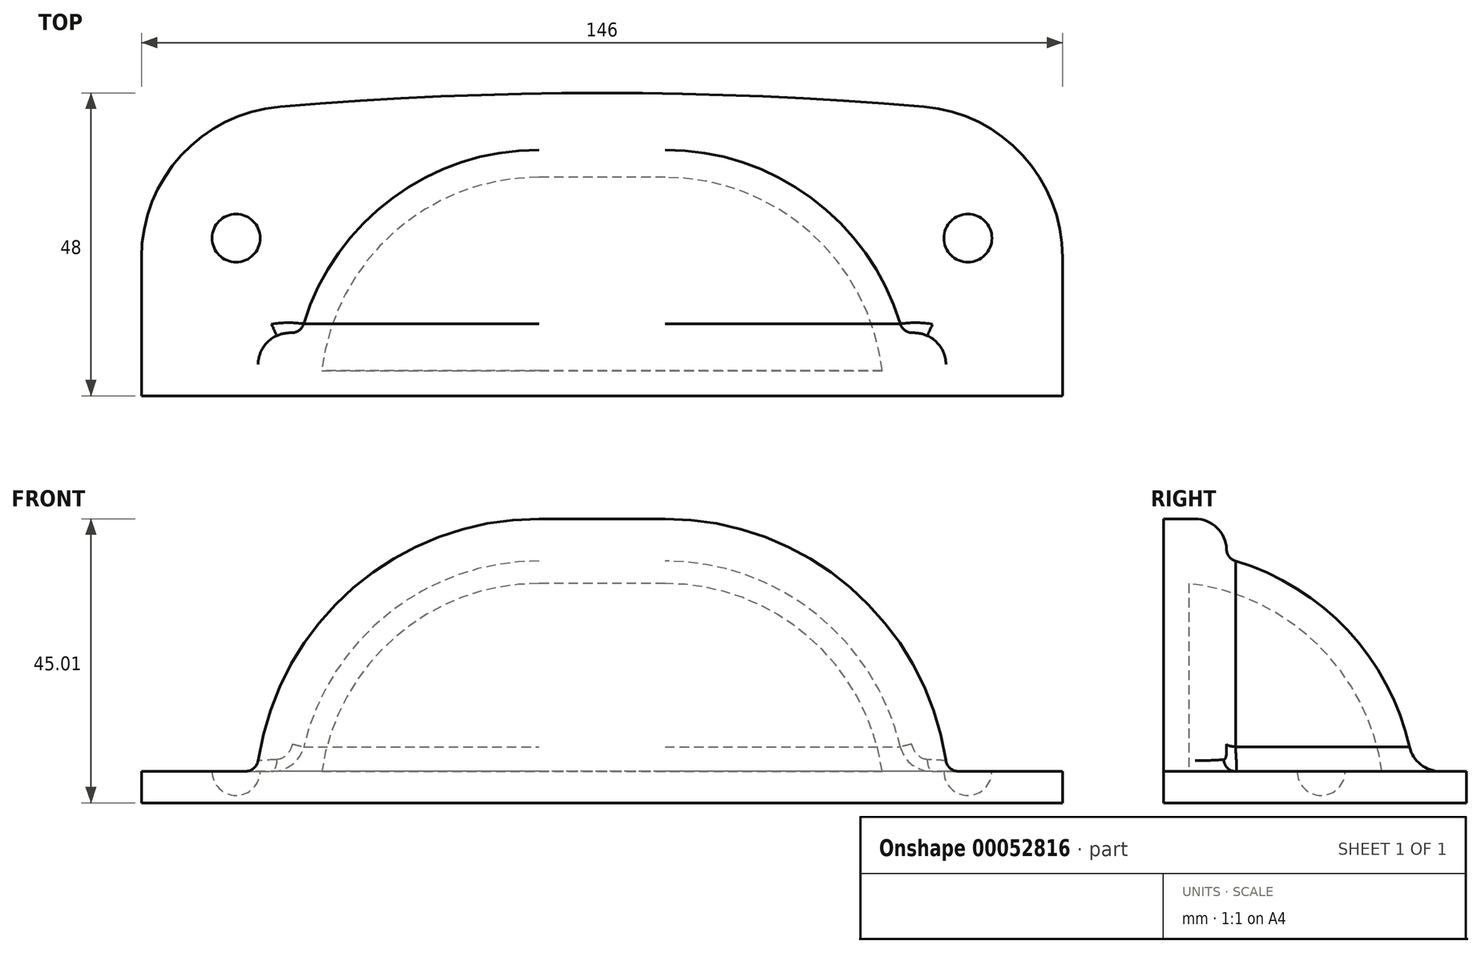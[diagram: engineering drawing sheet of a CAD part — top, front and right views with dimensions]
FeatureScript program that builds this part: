
annotation { "Feature Type Name" : "Feature", "Feature Type Description" : "" }
export const myFeature = defineFeature(function(context is Context, id is Id, definition is map)
    precondition{}
    {
        {
            var Q0;
            Q0=qCreatedBy(makeId("Top.planeOp"),FACE);
            var sketch = newSketch(context, id + "F0", { "sketchPlane" : qUnion([Q0])});
            skLineSegment(sketch, "E0", {"start": v(0, 0) * mm, "end": v(10, 0) * mm, "construction": true});
            skArc(sketch, "E1", {"start": v(10, 35) * mm, "mid": v(34.75, 24.75) * mm, "end": v(45, 0) * mm});
            skLineSegment(sketch, "E2", {"start": v(10, 35) * mm, "end": v(0, 35) * mm});
            skLineSegment(sketch, "E3", {"start": v(45, 0) * mm, "end": v(50, 0) * mm});
            skLineSegment(sketch, "E4.0", {"start": v(10, 40) * mm, "end": v(0, 40) * mm});
            skArc(sketch, "E4.1", {"start": v(10, 40) * mm, "mid": v(38.28, 28.28) * mm, "end": v(50, 0) * mm});
            skLineSegment(sketch, "E5", {"start": v(0, 40) * mm, "end": v(0, 0) * mm, "construction": true});
            skLineSegment(sketch, "E6.MirrorCS", {"start": v(-10, 35) * mm, "end": v(0, 35) * mm});
            skArc(sketch, "E7.MirrorCS", {"start": v(-10, 35) * mm, "mid": v(-34.75, 24.75) * mm, "end": v(-45, 0) * mm});
            skLineSegment(sketch, "E8.MirrorCS", {"start": v(-45, 0) * mm, "end": v(-50, 0) * mm});
            skArc(sketch, "E9.MirrorCS", {"start": v(-10, 40) * mm, "mid": v(-38.28, 28.28) * mm, "end": v(-50, 0) * mm});
            skLineSegment(sketch, "E10.MirrorCS", {"start": v(-10, 40) * mm, "end": v(0, 40) * mm});
            skLineSegment(sketch, "E11.MirrorCS", {"start": v(0, 0) * mm, "end": v(-10, 0) * mm});
            skSolve(sketch);
        }
        {
            var Q0;
            Q0=qSketchRegion(id+"F0",true);
            var Q1;
            Q1=sQuery(id+"F0.wireOp",EDGE,"E0");
            revolve(context, id + "F1", {"entities" : qUnion([Q0]), "axis" : qUnion([Q1]), "revolveType" : RevolveType.ONE_DIRECTION, "angle" : 90 * degree});
        }
        {
            var Q0;
            Q0=qCreatedBy(makeId("Top.planeOp"),FACE);
            var sketch = newSketch(context, id + "F2", { "sketchPlane" : qUnion([Q0])});
            skArc(sketch, "E12", {"start": v(51.04, 45.83) * mm, "mid": v(25.54, 47.46) * mm, "end": v(0, 48) * mm});
            skLineSegment(sketch, "E13", {"start": v(0, 0) * mm, "end": v(0, 48) * mm, "construction": true});
            skLineSegment(sketch, "E14", {"start": v(0, 48) * mm, "end": v(-79.99, 48) * mm, "construction": true});
            skLineSegment(sketch, "E15", {"start": v(0, 0) * mm, "end": v(10, 0) * mm});
            skLineSegment(sketch, "E16", {"start": v(73, 0) * mm, "end": v(73, 21.91) * mm});
            skPoint(sketch, "E17.visualSharp", {"position": v(73, 43.54) * mm});
            skArc(sketch, "E17.filletArc", {"start": v(73, 21.91) * mm, "mid": v(66.68, 38.14) * mm, "end": v(51.04, 45.83) * mm});
            skArc(sketch, "E18.MirrorCS", {"start": v(-51.04, 45.83) * mm, "mid": v(-25.54, 47.46) * mm, "end": v(0, 48) * mm});
            skArc(sketch, "E19.MirrorCS", {"start": v(-73, 21.91) * mm, "mid": v(-66.68, 38.14) * mm, "end": v(-51.04, 45.83) * mm});
            skLineSegment(sketch, "E20.MirrorCS", {"start": v(-73, 0) * mm, "end": v(-73, 21.91) * mm});
            skLineSegment(sketch, "E21.MirrorCS", {"start": v(0, 0) * mm, "end": v(-10, 0) * mm});
            skArc(sketch, "E22.0", {"start": v(-10, 35) * mm, "mid": v(-34.75, 24.75) * mm, "end": v(-45, 0) * mm});
            skLineSegment(sketch, "E22.1", {"start": v(10, 35) * mm, "end": v(-10, 35) * mm});
            skArc(sketch, "E22.2", {"start": v(10, 35) * mm, "mid": v(34.75, 24.75) * mm, "end": v(45, 0) * mm});
            skLineSegment(sketch, "E23.trimOffspring", {"start": v(-45, 0) * mm, "end": v(-73, 0) * mm});
            skLineSegment(sketch, "E24.trimOffspring", {"start": v(45, 0) * mm, "end": v(73, 0) * mm});
            skSolve(sketch);
        }
        {
            var Q0;
            Q0=qSketchRegion(id+"F2",true);
            extrude(context, id + "F3", {"entities" : qUnion([Q0]), "operationType" : NewBodyOperationType.ADD, "depth" : 5 * mm});
        }
        {
            var Q0;
            Q0=qCreatedBy(makeId("Right.planeOp"),FACE);
            var sketch = newSketch(context, id + "F4", { "sketchPlane" : qUnion([Q0])});
            skArc(sketch, "E25.0.0", {"start": v(10, 33.54) * mm, "mid": v(5.05, 34.63) * mm, "end": v(0, 35) * mm});
            skArc(sketch, "E25.0.2", {"start": v(0, 35) * mm, "mid": v(5.05, 34.63) * mm, "end": v(10, 33.54) * mm});
            skLineSegment(sketch, "E26", {"start": v(0, 35) * mm, "end": v(0, 40) * mm});
            skArc(sketch, "E27", {"start": v(5, 45) * mm, "mid": v(8.54, 43.54) * mm, "end": v(10, 40) * mm});
            skLineSegment(sketch, "E28", {"start": v(10, 40) * mm, "end": v(10, 33.54) * mm});
            skPoint(sketch, "E29.orphan", {"position": v(35, 0) * mm});
            skLineSegment(sketch, "E30", {"start": v(5, 40) * mm, "end": v(5, 45) * mm, "construction": true});
            skLineSegment(sketch, "E31", {"start": v(5, 45) * mm, "end": v(0, 45) * mm});
            skLineSegment(sketch, "E32", {"start": v(0, 45) * mm, "end": v(0, 40) * mm});
            skSolve(sketch);
        }
        {
            var Q0;
            Q0=makeQuery(id+"F3.boolean.opBoolean","MERGE",FACE,{"derivedFrom":[makeQuery(id+"F1.opRevolve","CAP_FACE",FACE,{"disambiguationData":[OSD([sQuery(id+"F0.wireOp",EDGE,"E1"),sQuery(id+"F0.wireOp",EDGE,"E2"),sQuery(id+"F0.wireOp",EDGE,"E3"),sQuery(id+"F0.wireOp",EDGE,"E4.0"),sQuery(id+"F0.wireOp",EDGE,"E4.1"),sQuery(id+"F0.wireOp",EDGE,"E6.MirrorCS"),sQuery(id+"F0.wireOp",EDGE,"E7.MirrorCS"),sQuery(id+"F0.wireOp",EDGE,"E8.MirrorCS"),sQuery(id+"F0.wireOp",EDGE,"E9.MirrorCS"),sQuery(id+"F0.wireOp",EDGE,"E10.MirrorCS")])],"isStart":false}),makeQuery(id+"F3.opExtrude","SWEPT_FACE",FACE,{"disambiguationData":[OSD([sQuery(id+"F2.wireOp",EDGE,"E23.trimOffspring")])]}),makeQuery(id+"F3.opExtrude","SWEPT_FACE",FACE,{"disambiguationData":[OSD([sQuery(id+"F2.wireOp",EDGE,"E24.trimOffspring")])]})]});
            var sketch = newSketch(context, id + "F5", { "sketchPlane" : qUnion([Q0])});
            skLineSegment(sketch, "E33.0", {"start": v(10, 35) * mm, "end": v(0, 35) * mm});
            skArc(sketch, "E33.1", {"start": v(10, 35) * mm, "mid": v(34.75, 24.75) * mm, "end": v(45, 0) * mm});
            skLineSegment(sketch, "E34", {"start": v(0, 0) * mm, "end": v(0, 35) * mm, "construction": true});
            skPoint(sketch, "E35.orphan", {"position": v(-10, 35) * mm});
            skSolve(sketch);
        }
        {
            var Q0;
            Q0=qSketchRegion(id+"F4",true);
            var Q1;
            Q1=qConstructionFilter(qBodyType(qCreatedBy(id+"F5",EDGE),BodyType.WIRE),ConstructionObject.NO);
            sweep(context, id + "F6", {"profiles" : qUnion([Q0]), "path" : qUnion([Q1])});
        }
        {
            var Q0;
            Q0=makeQuery(id+"F3.boolean.opBoolean","INTERSECT",EDGE,{"derivedFrom":[makeQuery(id+"F1.opRevolve","SWEPT_FACE",FACE,{"disambiguationData":[OSD([sQuery(id+"F0.wireOp",EDGE,"E9.MirrorCS")])]}),makeQuery(id+"F3.opExtrude","CAP_FACE",FACE,{"disambiguationData":[OSD([sQuery(id+"F2.wireOp",EDGE,"E12"),sQuery(id+"F2.wireOp",EDGE,"E15"),sQuery(id+"F2.wireOp",EDGE,"E16"),sQuery(id+"F2.wireOp",EDGE,"E17.filletArc"),sQuery(id+"F2.wireOp",EDGE,"E18.MirrorCS"),sQuery(id+"F2.wireOp",EDGE,"E19.MirrorCS"),sQuery(id+"F2.wireOp",EDGE,"E20.MirrorCS"),sQuery(id+"F2.wireOp",EDGE,"E21.MirrorCS")])],"isStart":false})]});
            fillet(context, id + "F7", {"entities" : qUnion([Q0]), "radius" : 5 * mm, "tangentPropagation" : true, "allowEdgeOverflow" : false});
        }
        {
            var Q0;
            Q0=makeQuery(id+"F6.opSweep","SWEPT_BODY",BODY,{"disambiguationData":[OSD([sQuery(id+"F4.wireOp",EDGE,"E25.0.2"),sQuery(id+"F4.wireOp",EDGE,"E26"),sQuery(id+"F4.wireOp",EDGE,"E27"),sQuery(id+"F4.wireOp",EDGE,"E28"),sQuery(id+"F5.wireOp",EDGE,"E33.1")])]});
            var Q1;
            Q1=qCreatedBy(makeId("Right.planeOp"),FACE);
            mirror(context, id + "F8", {"entities" : qUnion([Q0]), "mirrorPlane" : qUnion([Q1])});
        }
        {
            var Q0;
            Q0=makeQuery(id+"F1.opRevolve","SWEPT_BODY",BODY,{"disambiguationData":[OSD([sQuery(id+"F0.wireOp",EDGE,"E1"),sQuery(id+"F0.wireOp",EDGE,"E2"),sQuery(id+"F0.wireOp",EDGE,"E3"),sQuery(id+"F0.wireOp",EDGE,"E4.0"),sQuery(id+"F0.wireOp",EDGE,"E4.1"),sQuery(id+"F0.wireOp",EDGE,"E6.MirrorCS"),sQuery(id+"F0.wireOp",EDGE,"E7.MirrorCS"),sQuery(id+"F0.wireOp",EDGE,"E8.MirrorCS"),sQuery(id+"F0.wireOp",EDGE,"E9.MirrorCS"),sQuery(id+"F0.wireOp",EDGE,"E10.MirrorCS")])]});
            var Q1;
            Q1=makeQuery(id+"F8.opPattern","COPY",BODY,{"derivedFrom":makeQuery(id+"F6.opSweep","SWEPT_BODY",BODY,{"disambiguationData":[OSD([sQuery(id+"F4.wireOp",EDGE,"E25.0.2"),sQuery(id+"F4.wireOp",EDGE,"E26"),sQuery(id+"F4.wireOp",EDGE,"E27"),sQuery(id+"F4.wireOp",EDGE,"E28"),sQuery(id+"F5.wireOp",EDGE,"E33.1")])]}),"instanceName":"1"});
            var Q2;
            Q2=makeQuery(id+"F6.opSweep","SWEPT_BODY",BODY,{"disambiguationData":[OSD([sQuery(id+"F4.wireOp",EDGE,"E25.0.2"),sQuery(id+"F4.wireOp",EDGE,"E26"),sQuery(id+"F4.wireOp",EDGE,"E27"),sQuery(id+"F4.wireOp",EDGE,"E28"),sQuery(id+"F5.wireOp",EDGE,"E33.1")])]});
            booleanBodies(context, id + "F9", {"operationType" : BooleanOperationType.UNION, "tools" : qUnion([Q0, Q1, Q2])});
        }
        {
            var Q0;
            Q0=makeQuery(id+"F9.opBoolean","INTERSECT",EDGE,{"derivedFrom":[makeQuery(id+"F6.opSweep","SWEPT_FACE",FACE,{"disambiguationData":[OSD([sQuery(id+"F4.wireOp",EDGE,"E28"),sQuery(id+"F5.wireOp",EDGE,"E33.0")])]}),makeQuery(id+"F1.opRevolve","SWEPT_FACE",FACE,{"disambiguationData":[OSD([sQuery(id+"F0.wireOp",EDGE,"E9.MirrorCS")])]})]});
            var Q1;
            {var subQ0=makeQuery(id+"F6.opSweep","SWEPT_EDGE",EDGE,{"disambiguationData":[OSD([sQuery(id+"F4.wireOp",EDGE,"E27"),sQuery(id+"F4.wireOp",EDGE,"E28"),sQuery(id+"F5.wireOp",EDGE,"E33.0")])]});Q1=makeQuery(id+"F9.opBoolean","MERGE",EDGE,{"derivedFrom":[subQ0,makeQuery(id+"F8.opPattern","COPY",EDGE,{"derivedFrom":subQ0,"instanceName":"1"})]});}
            var Q2;
            Q2=makeQuery(id+"F6.opSweep","SWEPT_EDGE",EDGE,{"disambiguationData":[OSD([sQuery(id+"F4.wireOp",EDGE,"E27"),sQuery(id+"F4.wireOp",EDGE,"E28"),sQuery(id+"F5.wireOp",EDGE,"E33.1")])]});
            var Q3;
            Q3=makeQuery(id+"F9.opBoolean","INTERSECT",EDGE,{"derivedFrom":[makeQuery(id+"F7.opFillet","BLEND_FACE",FACE,{"disambiguationData":[OSD([sQuery(id+"F0.wireOp",EDGE,"E9.MirrorCS"),sQuery(id+"F2.wireOp",EDGE,"E12"),sQuery(id+"F2.wireOp",EDGE,"E16"),sQuery(id+"F2.wireOp",EDGE,"E17.filletArc"),sQuery(id+"F2.wireOp",EDGE,"E18.MirrorCS"),sQuery(id+"F2.wireOp",EDGE,"E19.MirrorCS"),sQuery(id+"F2.wireOp",EDGE,"E20.MirrorCS"),sQuery(id+"F2.wireOp",EDGE,"E22.0"),sQuery(id+"F2.wireOp",EDGE,"E22.1"),sQuery(id+"F2.wireOp",EDGE,"E22.2"),sQuery(id+"F2.wireOp",EDGE,"E23.trimOffspring"),sQuery(id+"F2.wireOp",EDGE,"E24.trimOffspring")])]}),makeQuery(id+"F8.opPattern","COPY",FACE,{"derivedFrom":makeQuery(id+"F6.opSweep","SWEPT_FACE",FACE,{"disambiguationData":[OSD([sQuery(id+"F4.wireOp",EDGE,"E27"),sQuery(id+"F5.wireOp",EDGE,"E33.1")])]}),"instanceName":"1"})]});
            var Q4;
            Q4=makeQuery(id+"F8.opPattern","COPY",EDGE,{"derivedFrom":makeQuery(id+"F6.opSweep","SWEPT_EDGE",EDGE,{"disambiguationData":[OSD([sQuery(id+"F4.wireOp",EDGE,"E27"),sQuery(id+"F4.wireOp",EDGE,"E28"),sQuery(id+"F5.wireOp",EDGE,"E33.1")])]}),"instanceName":"1"});
            var Q5;
            Q5=makeQuery(id+"F9.opBoolean","INTERSECT",EDGE,{"derivedFrom":[makeQuery(id+"F6.opSweep","SWEPT_FACE",FACE,{"disambiguationData":[OSD([sQuery(id+"F4.wireOp",EDGE,"E27"),sQuery(id+"F5.wireOp",EDGE,"E33.1")])]}),makeQuery(id+"F7.opFillet","BLEND_FACE",FACE,{"disambiguationData":[OSD([sQuery(id+"F0.wireOp",EDGE,"E4.1"),sQuery(id+"F2.wireOp",EDGE,"E12"),sQuery(id+"F2.wireOp",EDGE,"E16"),sQuery(id+"F2.wireOp",EDGE,"E17.filletArc"),sQuery(id+"F2.wireOp",EDGE,"E18.MirrorCS"),sQuery(id+"F2.wireOp",EDGE,"E19.MirrorCS"),sQuery(id+"F2.wireOp",EDGE,"E20.MirrorCS"),sQuery(id+"F2.wireOp",EDGE,"E22.0"),sQuery(id+"F2.wireOp",EDGE,"E22.1"),sQuery(id+"F2.wireOp",EDGE,"E22.2"),sQuery(id+"F2.wireOp",EDGE,"E23.trimOffspring"),sQuery(id+"F2.wireOp",EDGE,"E24.trimOffspring")])]})]});
            fillet(context, id + "F10", {"entities" : qUnion([Q0, Q1, Q2, Q3, Q4, Q5]), "radius" : 2 * mm, "tangentPropagation" : true, "allowEdgeOverflow" : false});
        }
        {
            var Q0;
            Q0=makeQuery(id+"F3.opExtrude","CAP_FACE",FACE,{"disambiguationData":[OSD([sQuery(id+"F2.wireOp",EDGE,"E12"),sQuery(id+"F2.wireOp",EDGE,"E16"),sQuery(id+"F2.wireOp",EDGE,"E17.filletArc"),sQuery(id+"F2.wireOp",EDGE,"E18.MirrorCS"),sQuery(id+"F2.wireOp",EDGE,"E19.MirrorCS"),sQuery(id+"F2.wireOp",EDGE,"E20.MirrorCS"),sQuery(id+"F2.wireOp",EDGE,"E22.0"),sQuery(id+"F2.wireOp",EDGE,"E22.1"),sQuery(id+"F2.wireOp",EDGE,"E22.2"),sQuery(id+"F2.wireOp",EDGE,"E23.trimOffspring"),sQuery(id+"F2.wireOp",EDGE,"E24.trimOffspring")])],"isStart":false});
            var sketch = newSketch(context, id + "F11", { "sketchPlane" : qUnion([Q0])});
            skArc(sketch, "E36", {"start": v(58, 21.19) * mm, "mid": v(61.81, 25) * mm, "end": v(58, 28.81) * mm});
            skLineSegment(sketch, "E37", {"start": v(58, 25) * mm, "end": v(58, 37.6) * mm, "construction": true});
            skLineSegment(sketch, "E38", {"start": v(58, 25) * mm, "end": v(58, 28.81) * mm});
            skLineSegment(sketch, "E39", {"start": v(58, 25) * mm, "end": v(58, 21.19) * mm});
            skSolve(sketch);
        }
        {
            var Q0;
            Q0=makeQuery(id+"F11.imprint","IMPRINT",FACE,{"disambiguationData":[TD([[makeQuery(id+"F11.imprint","IMPRINT",EDGE,{"derivedFrom":sQuery(id+"F11.wireOp",EDGE,"E36")}),1.0]])]});
            var Q1;
            Q1=sQuery(id+"F11.wireOp",EDGE,"E37");
            revolve(context, id + "F12", {"entities" : qUnion([Q0]), "axis" : qUnion([Q1]), "revolveType" : RevolveType.FULL});
        }
        {
            var Q0;
            Q0=makeQuery(id+"F12.opRevolve","SWEPT_BODY",BODY,{"disambiguationData":[OSD([sQuery(id+"F11.wireOp",EDGE,"E36"),sQuery(id+"F11.wireOp",EDGE,"E38"),sQuery(id+"F11.wireOp",EDGE,"E39")])]});
            var Q1;
            Q1=qCreatedBy(makeId("Right.planeOp"),FACE);
            mirror(context, id + "F13", {"entities" : qUnion([Q0]), "mirrorPlane" : qUnion([Q1])});
        }
        {
            var Q0;
            Q0=makeQuery(id+"F13.opPattern","COPY",BODY,{"derivedFrom":makeQuery(id+"F12.opRevolve","SWEPT_BODY",BODY,{"disambiguationData":[OSD([sQuery(id+"F11.wireOp",EDGE,"E36"),sQuery(id+"F11.wireOp",EDGE,"E38"),sQuery(id+"F11.wireOp",EDGE,"E39")])]}),"instanceName":"1"});
            var Q1;
            Q1=makeQuery(id+"F12.opRevolve","SWEPT_BODY",BODY,{"disambiguationData":[OSD([sQuery(id+"F11.wireOp",EDGE,"E36"),sQuery(id+"F11.wireOp",EDGE,"E38"),sQuery(id+"F11.wireOp",EDGE,"E39")])]});
            var Q2;
            Q2=makeQuery(id+"F1.opRevolve","SWEPT_BODY",BODY,{"disambiguationData":[OSD([sQuery(id+"F0.wireOp",EDGE,"E1"),sQuery(id+"F0.wireOp",EDGE,"E2"),sQuery(id+"F0.wireOp",EDGE,"E3"),sQuery(id+"F0.wireOp",EDGE,"E4.0"),sQuery(id+"F0.wireOp",EDGE,"E4.1"),sQuery(id+"F0.wireOp",EDGE,"E6.MirrorCS"),sQuery(id+"F0.wireOp",EDGE,"E7.MirrorCS"),sQuery(id+"F0.wireOp",EDGE,"E8.MirrorCS"),sQuery(id+"F0.wireOp",EDGE,"E9.MirrorCS"),sQuery(id+"F0.wireOp",EDGE,"E10.MirrorCS")])]});
            booleanBodies(context, id + "F14", {"operationType" : BooleanOperationType.SUBTRACTION, "tools" : qUnion([Q0, Q1]), "targets" : qUnion([Q2])});
        }
        {
            var Q0;
            Q0=qCreatedBy(makeId("Top.planeOp"),FACE);
            var sketch = newSketch(context, id + "F15", { "sketchPlane" : qUnion([Q0])});
            skArc(sketch, "E40.0", {"start": v(-10, 35) * mm, "mid": v(-34.75, 24.75) * mm, "end": v(-45, 0) * mm});
            skLineSegment(sketch, "E40.1", {"start": v(10, 35) * mm, "end": v(-10, 35) * mm});
            skArc(sketch, "E40.2", {"start": v(10, 35) * mm, "mid": v(34.75, 24.75) * mm, "end": v(45, 0) * mm});
            skLineSegment(sketch, "E41", {"start": v(-45, 0) * mm, "end": v(45, 0) * mm});
            skSolve(sketch);
        }
        {
            var Q0;
            Q0=qSketchRegion(id+"F15",true);
            extrude(context, id + "F16", {"entities" : qUnion([Q0]), "operationType" : NewBodyOperationType.ADD, "depth" : 5 * mm});
        }
        {
            var Q0;
            Q0=qCreatedBy(makeId("Front.planeOp"),FACE);
            var sketch = newSketch(context, id + "F17", { "sketchPlane" : qUnion([Q0])});
            skLineSegment(sketch, "E42.0", {"start": v(10, 37) * mm, "end": v(-10, 37) * mm});
            skArc(sketch, "E42.1", {"start": v(10, 37) * mm, "mid": v(35.08, 27.2) * mm, "end": v(46.88, 3) * mm});
            skLineSegment(sketch, "E42.2", {"start": v(-46.88, 3) * mm, "end": v(46.88, 3) * mm});
            skArc(sketch, "E42.3", {"start": v(-10, 37) * mm, "mid": v(-35.08, 27.2) * mm, "end": v(-46.88, 3) * mm});
            skSolve(sketch);
        }
        {
            var Q0;
            Q0 = qSketchRegion(id + "F17", true);
            extrude(context, id + "F18", {"entities" : qUnion([Q0]), "operationType" : NewBodyOperationType.ADD, "oppositeDirection" : true, "depth" : 4 * mm});
        }
    });
